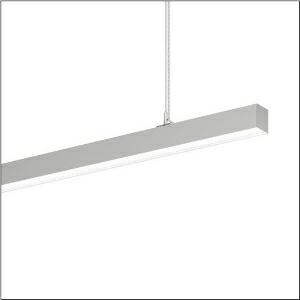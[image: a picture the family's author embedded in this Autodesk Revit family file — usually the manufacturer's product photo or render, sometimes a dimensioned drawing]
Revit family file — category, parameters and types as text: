
# Revit family: silica_r__21_51mx30dc49sb_4188
name_source: partatom
category: Lighting Fixtures
units: mm (PartAtom-declared; Revit-internal decimal feet)

## family parameters
Cut with Voids When Loaded = No
Host = Face
Light Source = No
Part Type = Normal
Room Calculation Point = No
Round Connector Dimension = Use Diameter
Shared = No

## types (1)
- --- (1 x LED, 10520 lm, 64.1 W, 4000K)
    Apparent Load = 64 VA
    CIE Flux Codes = 47 79 96 57 100
    Color Rendering = 80
    Color Temperature = 4000K
    Default Elevation = 1800 mm
    Description = Silica® 21, office luminaire, primary optical cover: cover, of PMMA, opal, light emission: direct/indirect distribution, primary light characteristic: symmetric, installation type: suspended mounting, LED, rated luminous flux: 10.520lm, luminous efficacy: 164lm/W, light colour: 840, colour temperature: 4000K, control gear: DALI 2, with terminal, 3+2-pole, max. 2.5mm², mains connection: 220..240V, AC, 50/60Hz, rated input power: 64.1W, luminaire housing, of aluminium, metallic grey (RAL 9006), length: 3.004mm, width: 53mm, height: 53mm, protection rating (complete): IP20, insulation class (complete): insulation class I (protective earthing), certification: CE, permissible operating ambient temperature: 0..+35°C, standard: EN 50419, packaging unit: 1 piece
    Height = 53 mm
    Lamp = 1 x LED
    Lamp Light Flux = 10520 lm
    Lamp Power = 64.1 W
    Lamp count = 1
    Length = 3004 mm
    Luminous efficacy = 164 lm/W
    Manufacturer = Siteco
    ModVariant = No
    Model = 51MX30DC49SB
    Mounting Place = Ceiling
    Mounting Type = Pendant
    Number of Poles = 1
    OnlyDefault = Yes
    Power Factor = 1
    Product Name = Silica® 21
    Product group = office luminaire | ceiling pendant
    ProductGroupID = 904
    Protection Class = Protection class I
    Protection Degree = IP 20
    RLX_Detail_Level = 1
    RLX_Emergency_Light_Flux = 0 lm
    RLX_Emergency_Type = 0
    RLX_Emergency_Type_DB = No
    RlxData = <blob elided: 23357 chars, md5=1db6c981>
    Socket = socket
    Standby Power = 0 W
    System Light Flux = 10520 lm
    System Power = 64 W
    Type Comments = factory setting: luminous flux: 100 % | dim-lin: 254 | 218 mA
    Type Image = l_1335864.jpg
    URL = http://relux.com
    VarID = @adj_117104
    Voltage = 0 V
    Weight = 0.00 kg
    Width = 53 mm

## geometry (parser evidence)
native form markers: Blend x4, Sweep x12
no freeform markers — native parametric forms only
